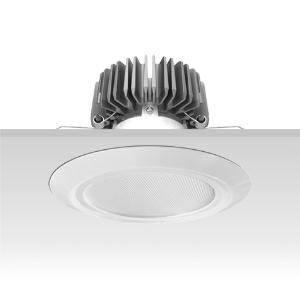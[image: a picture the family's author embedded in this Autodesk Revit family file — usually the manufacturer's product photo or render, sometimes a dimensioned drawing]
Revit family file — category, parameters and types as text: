
# Revit family: 3f_filippi_-_3f_reno_bianco_ampio_3f_filippi_-_30687_a01037_-_3f_reno_200_wh_4000-840_dali_wide___vs_wh_e4dc
name_source: partatom
category: Lighting Fixtures
units: mm (PartAtom-declared; Revit-internal decimal feet)

## family parameters
Cut with Voids When Loaded = No
Host = Face
Light Source = No
Part Type = Normal
Room Calculation Point = No
Round Connector Dimension = Use Diameter
Shared = No

## types (1)
- 3F Filippi - 3F Reno Bianco Ampio (1 x LED, 3089 lm, 36 W, 4000 K)
    Apparent Load = 36 VA
    Approval mark = CE
    CIE Flux Codes = 75 94 99 100 100
    Color Rendering = 80
    Color Temperature = 4000 K
    Control Gear = Electronic transformer
    Default Elevation = 1800 mm
    Description = ILLUMINOTECHNICAL
Luminous efficiency 100% (DLOR 100%, ULOR 0%).
Initial luminous flux of the luminaire 3089 lm.
Direct symmetric wide distribution.
Installation Interdistance Transv.D = 1.16 x hu - Long.D = 1.14 x hu.
Tabular UGR (CIE 117 - 4H-8H; S=0.25H; 70/50/20): RUG 22.5 - 22.4.
Beam angle: 74° - 74°.
Luminous efficacy 86 lm/W.
Lifetime (L90/B10): 30000 h. (tq+25°C)
Lifetime (L85/B10): 50000 h. (tq+25°C)
Lifetime (L70/B10): 80000 h. (tq+25°C)
Sudden decreased luminous flux after 50000 hours: 0% (C0).
Photobiological safety in compliance with IEC/TR 62778: RG1 low risk, (IEC 62471).
In compliance with IEC/EN 62722-2-1 - IEC/EN 62717 standards.

SOURCE
Compact LED module 4000/840.
Energy efficiency class (UE 2019/2020 - UE 2019/2015): D.
CIE 13.3 Colour rendering index: CRI >80 (R9 <50%).
IES TM-30 Fidelity Index: Rf = 84 Rg = 95.
CCT nominal colour temperature 4000 K.
Colour initial tolerance (MacAdam): SDCM 3.
Zhaga Book 3 compliant.

MECHANICAL
Passive heat dissipator in die-casting aluminium, oversized, for optimum thermal management of the LED module.
Parabolic element with graduated/concentric rings in white polycarbonate.
Transparent external lens with glossy and satin differentiated surfaces, with a cooling and anti-insect system in methacrylate (PMMA).
Fastening spring clips in stainless steel.
Dimensions: diameter 226 mm, height 146 mm. Weight 1.855 kg.
IP44 protection degree for exposed part, IP20 for recessed part.
Mechanical strength to impacts IK06 (1 joule).
Glow-wire test resistance 650°C.

ELECTRICAL
Wiring on a separate unit.
Halogen Free DALI-2 DATI (Parts 251, 252, 253), PUSH-DIM, electronic wiring 230V-50/60Hz, power factor 0.97 at full load, THD <25%, constant output current, SELV, class II, 1 driver, 1 DALI addresse.
Power of the luminaire 36 W.
ENEC - CE.
SAFE FLICKER: PstLM=<1 and SVM=<0.4 (IEC TR 61547-1 and IEC TR 63158), to ensure a more comfortable and safe light.
Luminaire compliant with EN 60598-2-22 for power supply from a centralised emergency system CPSS (Central Power Supply System), not incorporated in the luminaire - high risk areas excluded. The default power and flux are 100% in AC and 100% in DC.
Ambient temperature from 0°C to +25°C.
Temperature class T6 max 85°C.
Relative humidity UR: <85%.

INSTALLATION
Pull-up recessed fitting.
False ceiling carving: 200 mm.
All accessories dedicated to this product are available on the Catalog and on our website www.3F-Filippi.com.

ACCESSORIES
A01037 - Anti-glare microprismatic VS moulded glass, tempered, not flammable, locked and in line with the trim, in white polycarbonate.

APPLICATIONS
Environments: architectural, commercial, exhibition areas, transit areas, corridors, shops, display windows, service areas.
In false ceilings with narrow voids.

LIGHT MANAGEMENT
Recommended minimum setting: 10%.
The luminaire, equipped with (DALI-2 DATI) driver, can be controlled manually with 3F Easy Dim technology or automatically/manually with wired or wireless DALI/D2D control systems.
The D2D driver guarantees interoperability with other devices with the same certification by making the following information available:
Device Data (Part 251), Energy Report (Part 252), Diagnosis & Maintenance (Part 253).
In electrical systems without a regulation system (manual or automatic) and DALI bus, a suitable jumper must be made on the DA-DA terminals of the appliance.

WARNING
Luminaire designed for disposal/recycling at end-of-life.
Replaceable (LED only) light source by a professional. Replaceable control gear by a professional.
    Height = 0 mm  [stored 0 ft]
    Lamp = 1 x LED
    Lamp Light Flux = 3089 lm
    Lamp Power = 36 W
    Lamp count = 1
    Length = 226 mm
    Lifetime = 50000 h
    Luminous efficacy = 86 lm/W
    Manufacturer = 3F Filippi
    ModVariant = No
    Model = 3F Filippi - 30687+A01037 - 3F Reno 200 WH 4000-840 DALI WIDE + VS WH
    Mounting Place = Ceiling
    Mounting Type = Recessed
    Number of Poles = 1
    OnlyDefault = Yes
    Power Factor = 1
    Product Name = 3F Filippi - 3F Reno Bianco Ampio
    Product group = recessed luminaire
    ProductGroupID = 4
    Protection Class = Protection class II
    Protection Degree = IP 20
    RLX_Detail_Level = 1
    RLX_Emergency_Light_Flux = 0 lm
    RLX_Emergency_Type = 0
    RLX_Emergency_Type_DB = No
    RlxData = <blob elided: 96273 chars, md5=386f783e>
    Socket = socket
    Standby Power = 0 W
    System Light Flux = 3089 lm
    System Power = 36 W
    Type Comments = Product without accessories
    Type Image = 3ffilippi_3f_reno_200_wh_vs_smp.jpg
    URL = http://relux.com
    VarID = ---
    Voltage = 0 V
    Weight = 0.00 kg
    Width = 0 mm  [stored 0 ft]

note: [stored X ft] marks values corroborated as IEEE doubles in the binary element streams (Revit-internal decimal feet)

## geometry (parser evidence)
native form markers: Blend x4, Sweep x13
no freeform markers — native parametric forms only
